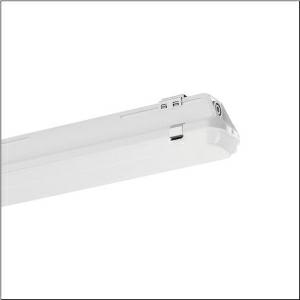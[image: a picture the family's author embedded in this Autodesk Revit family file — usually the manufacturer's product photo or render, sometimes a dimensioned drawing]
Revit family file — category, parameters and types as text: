
# Revit family: monsun_r__21_51fb10mp680c_b42b
name_source: partatom
category: Lighting Fixtures
units: mm (PartAtom-declared; Revit-internal decimal feet)

## family parameters
Cut with Voids When Loaded = No
Host = Face
Light Source = No
Part Type = Normal
Room Calculation Point = No
Round Connector Dimension = Use Diameter
Shared = No

## types (1)
- --- (1 x LED, 8200 lm, 46.9 W, 6500K)
    Apparent Load = 47 VA
    CIE Flux Codes = 47 77 93 94 100
    Color Rendering = 80
    Color Temperature = 6500K
    Default Elevation = 1800 mm
    Description = Monsun® 21, damp-proof luminaire, chain hanger, primary optical cover: enclosure, of PMMA, light emission: direct distribution, primary light characteristic: symmetric, installation type: suspended mounting, surface-mounted, horizontal mounting, vertical mounting, LED, rated luminous flux: 8.200lm, luminous efficacy: 175lm/W, light colour: 865, colour temperature: 6500K, control gear: ON/OFF Multilumen, with terminal, 3-pole, max. 2.5mm², mains connection: 220..240V, AC, 50/60Hz, rated input power: 47W, housing, of glass-fibre reinforced polyester, uncoated, bright grey, incl. chain hanger, length: 1.590mm, width: 90mm, height: 88mm, clip for enclosure, of stainless steel (V2A), ceiling mounting element, of stainless steel (V2A), chain hanger, of stainless steel (V2A), protection rating (complete): IP66, insulation class (complete): insulation class I (protective earthing), certification: CE, ENEC, VDE, UKCA, protection symbol: D, impact resistance: IK04, permissible operating ambient temperature: -25..+35°C, standard: EN 50419, EN 60598-2-1, corresponds to IFS (International Featured Standards) requirements for safety and quality in the food industry, for indoor or canopied outdoor use, no direct snow, no direct sun, no direct rain, LABS conformity tested according to VDMA 24364:2018-05, contact your sales advisor before using the luminaires in applications with unclear chemical exposure, large temperature fluctuations or condensation-forming humidity, packaging unit: 1 piece
    Height = 89 mm
    Lamp = 1 x LED
    Lamp Light Flux = 8200 lm
    Lamp Power = 46.9 W
    Lamp count = 1
    Length = 1590 mm
    Luminous efficacy = 175 lm/W
    Manufacturer = Siteco
    ModVariant = No
    Model = 51FB10MP680C
    Mounting Place = Ceiling
    Mounting Type = Surface mounted
    Number of Poles = 1
    OnlyDefault = Yes
    Power Factor = 1
    Product Name = Monsun® 21
    Product group = damp-proof luminaire
    ProductGroupID = 300
    Protection Class = Protection class I
    Protection Degree = IP 66
    RLX_Detail_Level = 1
    RLX_Emergency_Light_Flux = 0 lm
    RLX_Emergency_Type = 0
    RLX_Emergency_Type_DB = No
    RlxData = <blob elided: 89973 chars, md5=0cfadabd>
    Socket = socket
    Standby Power = 0 W
    System Light Flux = 8200 lm
    System Power = 47 W
    Type Comments = factory setting: luminous flux: 100 % | (A | C | E) | 109 mA
    Type Image = l_1319656.jpg
    URL = http://relux.com
    VarID = @adj_031778
    Voltage = 0 V
    Weight = 0.00 kg
    Width = 90 mm

## geometry (parser evidence)
native form markers: Blend x4, Sweep x13
no freeform markers — native parametric forms only
